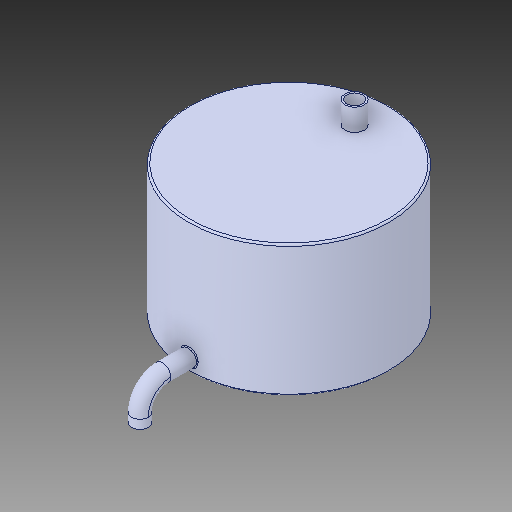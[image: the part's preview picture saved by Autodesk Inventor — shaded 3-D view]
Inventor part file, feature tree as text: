
AUTODESK INVENTOR PART (.ipt)
format: ipt  version: 2018 (Build 220112000, 112)  size: 372,736 bytes
history: native  units: in
note: dims shown in document units (in); Inventor stores cm internally (conversion verified against a paired STEP export)
features: shell x1
ambient origin geometry x8: Origin, YZ Plane, XZ Plane, XY Plane, X Axis, Y Axis, Z Axis, Center Point
bodies: Solid1 (feature_tree)
feature tree (1):
  shell  "Shell1"  [1 undecoded]
note: 1 required parameter value undecoded (feature->parameter linkage not recoverable at this tier; creation-order binding heuristic only, values carry confidence <= 0.55)
